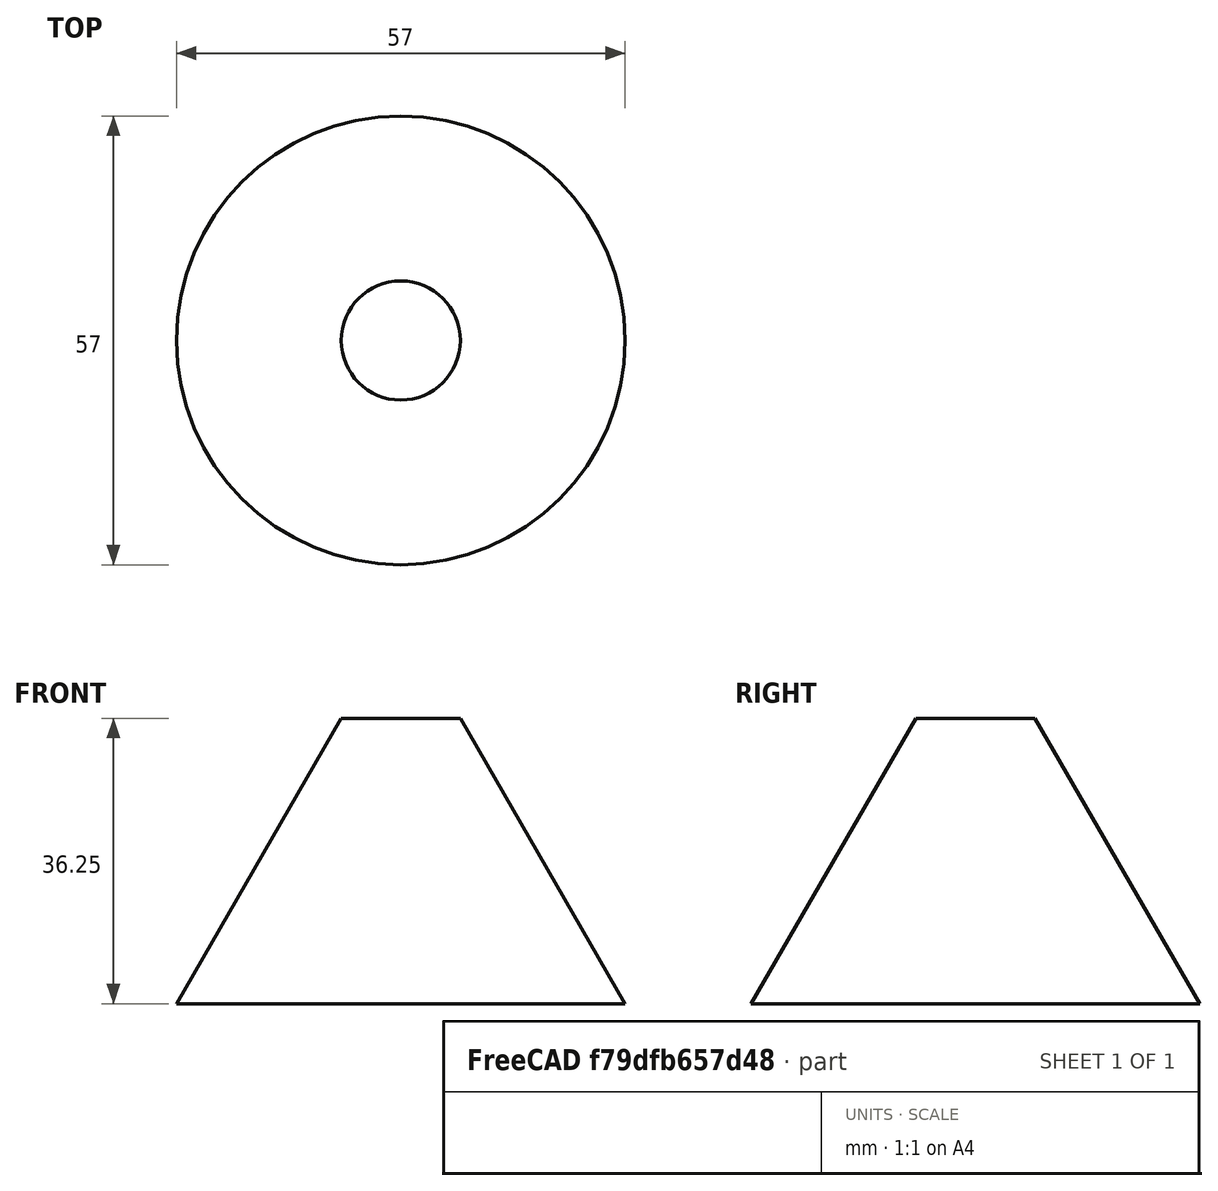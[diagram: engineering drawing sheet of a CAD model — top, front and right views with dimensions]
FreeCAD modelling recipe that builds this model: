
FCSTD DOCUMENT  (FreeCAD 0.20R29177 +426 (Git))
Label: fichaParchis
License: All rights reserved
LicenseURL: http://en.wikipedia.org/wiki/All_rights_reserved
objects: Sketcher::SketchObject×1, PartDesign::Revolution×1, PartDesign::Body×1
note: 4 computed .brp shape members not serialized (recipe doc carries the construction recipe); baked Part::Feature solids carry a one-line shape summary decoded from their .brp

FEATURE [Sketcher::SketchObject] Sketch
  FullyConstrained = true
  MapMode = 5
  Support = -> [XY_Plane]
  sketch-geometry (4):
    g0: LineSegment StartX=0 StartY=0 StartZ=0 EndX=28.5 EndY=0 EndZ=0
    g1: LineSegment StartX=28.5 StartY=0 StartZ=0 EndX=7.57 EndY=36.2518 EndZ=0
    g2: ArcOfCircle CenterX=1.62692 CenterY=41.6072 CenterZ=0 NormalX=0 NormalY=0 NormalZ=1 AngleXU=0 Radius=8 StartAngle=5.54976 EndAngle=8.05878
    g3: LineSegment StartX=9.548e-13 StartY=49.44 StartZ=0 EndX=0 EndY=0 EndZ=0
  constraints (13):
    c: PointOnObject(g0,g-2)
    c: PointOnObject(g0,g-1)
    c: Horizontal(g0)
    c: PointOnObject(g2,g-2)
    c: Coincident(g1,g0)
    c: Coincident(g3,g0)
    c: Coincident(g3,g2)
    c: Coincident(g2,g1)
    c: Angle(g1,g0) = 1.0472
    c: Radius(g2) = 8
    c: DistanceX(g0,g0) = 28.5
    c: DistanceX(g1,g1) = 20.93
    c: DistanceY(g3,g3) = 49.44
FEATURE [PartDesign::Revolution] Revolution
  Angle = 360
  Axis = (0,1,0)
  Base = (0,0,0)
  Profile = -> Sketch
  ReferenceAxis = -> Sketch [V_Axis]
  Reversed = true
FEATURE [PartDesign::Body] Body
  Group = -> [Sketch,Revolution]
  Origin = -> Origin
  Placement = pos=(0,0,0) rot=(1,0,0;1.5708rad)
  Tip = -> Revolution
